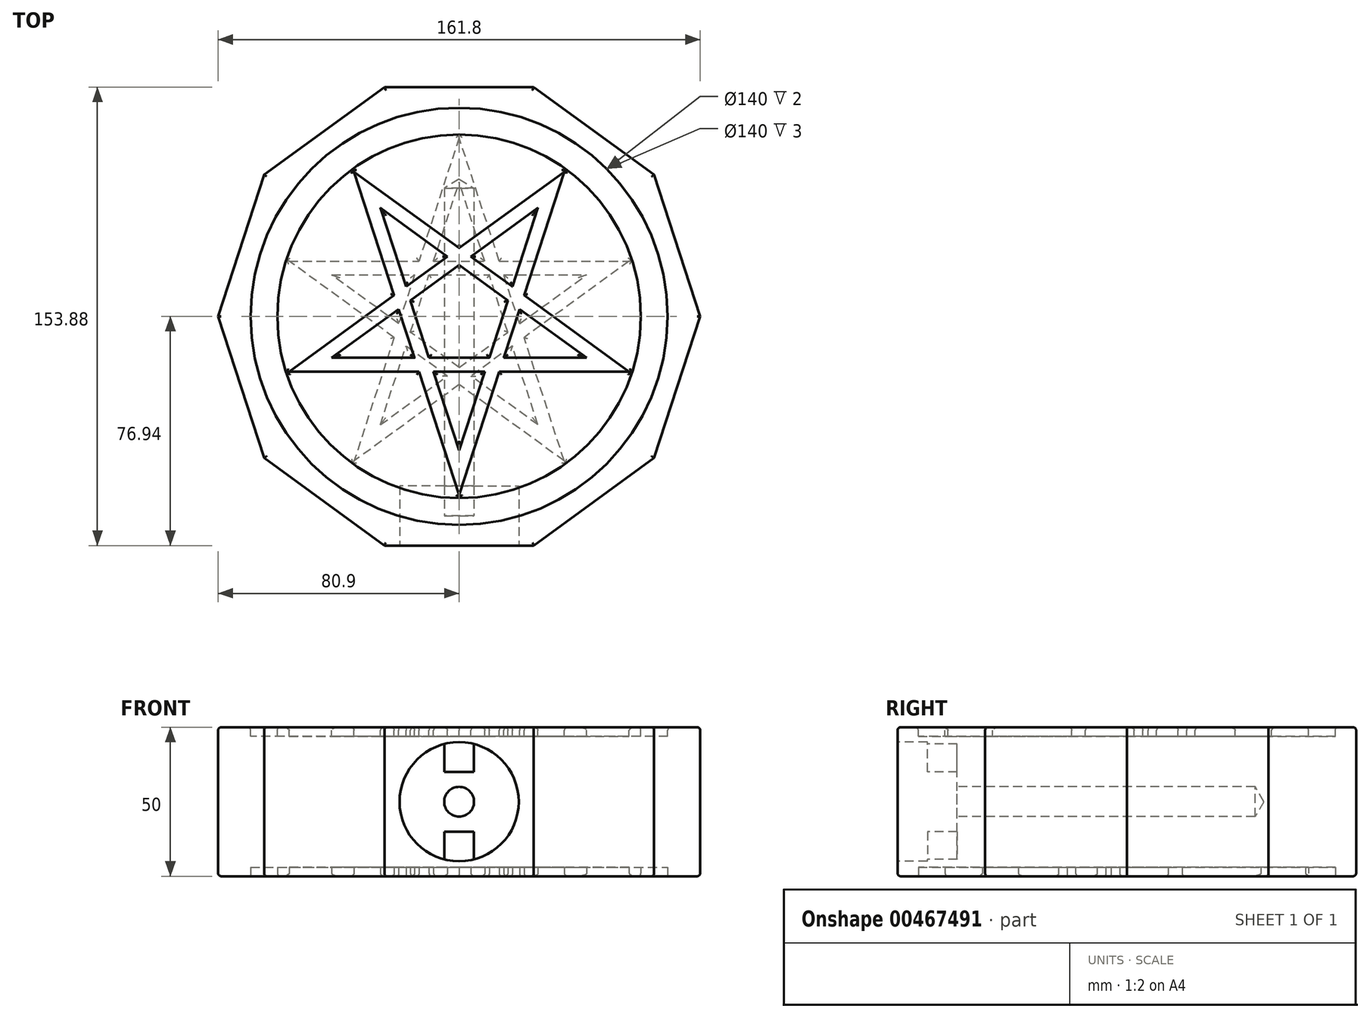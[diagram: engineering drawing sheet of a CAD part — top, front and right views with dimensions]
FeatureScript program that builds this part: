
annotation { "Feature Type Name" : "Feature", "Feature Type Description" : "" }
export const myFeature = defineFeature(function(context is Context, id is Id, definition is map)
    precondition{}
    {
        {
            var Q0;
            Q0=qCreatedBy(makeId("Top.planeOp"),FACE);
            var sketch = newSketch(context, id + "F0", { "sketchPlane" : qUnion([Q0])});
            skCircle(sketch, "E0.cCircle", {"center": v(0, 0) * mm, "radius": 80.9 * mm, "construction": true});
            skLineSegment(sketch, "E0.0", {"start": v(80.9, 0) * mm, "end": v(65.45, -47.55) * mm});
            skLineSegment(sketch, "E0.1", {"start": v(65.45, -47.55) * mm, "end": v(25, -76.94) * mm});
            skLineSegment(sketch, "E0.2", {"start": v(25, -76.94) * mm, "end": v(-25, -76.94) * mm});
            skLineSegment(sketch, "E0.3", {"start": v(-25, -76.94) * mm, "end": v(-65.45, -47.55) * mm});
            skLineSegment(sketch, "E0.4", {"start": v(-65.45, -47.55) * mm, "end": v(-80.9, 0) * mm});
            skLineSegment(sketch, "E0.5", {"start": v(-80.9, 0) * mm, "end": v(-65.45, 47.55) * mm});
            skLineSegment(sketch, "E0.6", {"start": v(-65.45, 47.55) * mm, "end": v(-25, 76.94) * mm});
            skLineSegment(sketch, "E0.7", {"start": v(-25, 76.94) * mm, "end": v(25, 76.94) * mm});
            skLineSegment(sketch, "E0.8", {"start": v(25, 76.94) * mm, "end": v(65.45, 47.55) * mm});
            skLineSegment(sketch, "E0.9", {"start": v(65.45, 47.55) * mm, "end": v(80.9, 0) * mm});
            skSolve(sketch);
        }
        {
            var Q0;
            Q0=makeQuery(id+"F0.imprint","IMPRINT",FACE,{"disambiguationData":[TD([[makeQuery(id+"F0.imprint","IMPRINT",EDGE,{"derivedFrom":sQuery(id+"F0.wireOp",EDGE,"E0.0")}),-1.0]])]});
            extrude(context, id + "F1", {"entities" : qUnion([Q0]), "depth" : 50 * mm});
        }
        {
            var Q0;
            Q0=makeQuery(id+"F1.opExtrude","SWEPT_FACE",FACE,{"disambiguationData":[OSD([sQuery(id+"F0.wireOp",EDGE,"E0.2")])]});
            var sketch = newSketch(context, id + "F2", { "sketchPlane" : qUnion([Q0])});
            skCircle(sketch, "E1", {"center": v(0, 25) * mm, "radius": 20 * mm});
            skLineSegment(sketch, "E2", {"start": v(0, 25) * mm, "end": v(0, 45) * mm, "construction": true});
            skLineSegment(sketch, "E3", {"start": v(0, 25) * mm, "end": v(0, 5) * mm, "construction": true});
            skLineSegment(sketch, "E4", {"start": v(0, 45) * mm, "end": v(0, 35) * mm});
            skLineSegment(sketch, "E5", {"start": v(0, 35) * mm, "end": v(5, 35) * mm});
            skLineSegment(sketch, "E6", {"start": v(5, 35) * mm, "end": v(5, 44.36) * mm});
            skLineSegment(sketch, "E7", {"start": v(0, 35) * mm, "end": v(-5, 35) * mm});
            skLineSegment(sketch, "E8", {"start": v(-5, 35) * mm, "end": v(-5, 44.36) * mm});
            skLineSegment(sketch, "E9", {"start": v(0, 5) * mm, "end": v(0, 15) * mm});
            skLineSegment(sketch, "E10", {"start": v(0, 15) * mm, "end": v(5, 15) * mm});
            skLineSegment(sketch, "E11", {"start": v(5, 15) * mm, "end": v(5, 5.64) * mm});
            skLineSegment(sketch, "E12", {"start": v(0, 15) * mm, "end": v(-5, 15) * mm});
            skLineSegment(sketch, "E13", {"start": v(-5, 15) * mm, "end": v(-5, 5.64) * mm});
            skSolve(sketch);
        }
        {
            var Q0;
            Q0=makeQuery(id+"F2.imprint","IMPRINT",FACE,{"disambiguationData":[TD([[makeQuery(id+"F2.imprint","IMPRINT",EDGE,{"derivedFrom":sQuery(id+"F2.wireOp",EDGE,"E5")}),-1.0]])]});
            extrude(context, id + "F3", {"entities" : qUnion([Q0]), "operationType" : NewBodyOperationType.REMOVE, "oppositeDirection" : true, "depth" : 20 * mm});
        }
        {
            var Q0;
            {var subQ0=sQuery(id+"F2.wireOp",EDGE,"E4");Q0=makeQuery(id+"F2.imprint","IMPRINT",FACE,{"disambiguationData":[TD([[makeQuery(id+"F2.imprint","IMPRINT",EDGE,{"derivedFrom":subQ0}),-1.0]])]});}
            var Q1;
            {var subQ0=sQuery(id+"F2.wireOp",EDGE,"E4");Q1=makeQuery(id+"F2.imprint","IMPRINT",FACE,{"disambiguationData":[TD([[makeQuery(id+"F2.imprint","IMPRINT",EDGE,{"derivedFrom":subQ0}),1.0]])]});}
            var Q2;
            {var subQ0=sQuery(id+"F2.wireOp",EDGE,"E9");Q2=makeQuery(id+"F2.imprint","IMPRINT",FACE,{"disambiguationData":[TD([[makeQuery(id+"F2.imprint","IMPRINT",EDGE,{"derivedFrom":subQ0}),1.0]])]});}
            var Q3;
            {var subQ0=sQuery(id+"F2.wireOp",EDGE,"E9");Q3=makeQuery(id+"F2.imprint","IMPRINT",FACE,{"disambiguationData":[TD([[makeQuery(id+"F2.imprint","IMPRINT",EDGE,{"derivedFrom":subQ0}),-1.0]])]});}
            extrude(context, id + "F4", {"entities" : qUnion([Q0, Q1, Q2, Q3]), "operationType" : NewBodyOperationType.REMOVE, "oppositeDirection" : true, "depth" : 10 * mm});
        }
        {
            var Q0;
            Q0=sQuery(id+"F2.wireOp",VERTEX,"E3.start");
            var Q1;
            Q1=makeQuery(id+"F1.opExtrude","SWEPT_BODY",BODY,{"disambiguationData":[OSD([sQuery(id+"F0.wireOp",EDGE,"E0.0"),sQuery(id+"F0.wireOp",EDGE,"E0.1"),sQuery(id+"F0.wireOp",EDGE,"E0.2"),sQuery(id+"F0.wireOp",EDGE,"E0.3"),sQuery(id+"F0.wireOp",EDGE,"E0.4"),sQuery(id+"F0.wireOp",EDGE,"E0.5"),sQuery(id+"F0.wireOp",EDGE,"E0.6"),sQuery(id+"F0.wireOp",EDGE,"E0.7"),sQuery(id+"F0.wireOp",EDGE,"E0.8"),sQuery(id+"F0.wireOp",EDGE,"E0.9")])]});
            hole(context, id + "F5", {"style" : HoleStyle.SIMPLE, "endStyle" : HoleEndStyle.BLIND, "holeDiameter" : 10 * mm, "holeDepth" : 100 * mm, "isTappedThrough" : true, "tappedDepth" : 12 * mm, "tapClearance" : 3, "locations" : qUnion([Q0]), "scope" : qUnion([Q1])});
        }
        {
            var Q0;
            Q0=makeQuery(id+"F1.opExtrude","CAP_FACE",FACE,{"disambiguationData":[OSD([sQuery(id+"F0.wireOp",EDGE,"E0.0"),sQuery(id+"F0.wireOp",EDGE,"E0.1"),sQuery(id+"F0.wireOp",EDGE,"E0.2"),sQuery(id+"F0.wireOp",EDGE,"E0.3"),sQuery(id+"F0.wireOp",EDGE,"E0.4"),sQuery(id+"F0.wireOp",EDGE,"E0.5"),sQuery(id+"F0.wireOp",EDGE,"E0.6"),sQuery(id+"F0.wireOp",EDGE,"E0.7"),sQuery(id+"F0.wireOp",EDGE,"E0.8"),sQuery(id+"F0.wireOp",EDGE,"E0.9")])],"isStart":false});
            var sketch = newSketch(context, id + "F6", { "sketchPlane" : qUnion([Q0])});
            skCircle(sketch, "E14.cCircle", {"center": v(0, 0) * mm, "radius": 60 * mm});
            skLineSegment(sketch, "E15", {"start": v(-42.8, -13.9) * mm, "end": v(42.8, -13.9) * mm});
            skLineSegment(sketch, "E16", {"start": v(-26.45, 36.4) * mm, "end": v(42.8, -13.9) * mm});
            skLineSegment(sketch, "E17", {"start": v(26.45, 36.4) * mm, "end": v(-42.8, -13.9) * mm});
            skLineSegment(sketch, "E18", {"start": v(-26.45, 36.4) * mm, "end": v(0, -45) * mm});
            skLineSegment(sketch, "E19", {"start": v(26.45, 36.4) * mm, "end": v(0, -45) * mm});
            skLineSegment(sketch, "E20", {"start": v(-57.06, -18.54) * mm, "end": v(57.06, -18.54) * mm});
            skLineSegment(sketch, "E21", {"start": v(57.06, -18.54) * mm, "end": v(-35.27, 48.54) * mm});
            skLineSegment(sketch, "E22", {"start": v(35.27, 48.54) * mm, "end": v(-57.06, -18.54) * mm});
            skLineSegment(sketch, "E23", {"start": v(35.27, 48.54) * mm, "end": v(0, -60) * mm});
            skLineSegment(sketch, "E24", {"start": v(0, -60) * mm, "end": v(-35.27, 48.54) * mm});
            skCircle(sketch, "E25", {"center": v(0, 0) * mm, "radius": 70 * mm});
            skCircle(sketch, "E26", {"center": v(0, 0) * mm, "radius": 61 * mm});
            skSolve(sketch);
        }
        {
            var Q0;
            Q0=makeQuery(id+"F6.imprint","IMPRINT",FACE,{"disambiguationData":[TD([[makeQuery(id+"F6.imprint","IMPRINT",EDGE,{"derivedFrom":sQuery(id+"F6.wireOp",EDGE,"E25")}),1.0]])]});
            var Q1;
            {var subQ5=sQuery(id+"F6.wireOp",EDGE,"E17");var subQ6=sQuery(id+"F6.wireOp",EDGE,"E15");var subQ7=makeQuery(id+"F6.imprint","INTERSECT",VERTEX,{"derivedFrom":[subQ6,subQ5]});Q1=makeQuery(id+"F6.imprint","IMPRINT",FACE,{"disambiguationData":[TD([[makeQuery(id+"F6.imprint","IMPRINT",EDGE,{"disambiguationData":[TD([[subQ7,-1.0]])],"derivedFrom":subQ6}),-1.0]])]});}
            var Q2;
            {var subQ1=sQuery(id+"F6.wireOp",EDGE,"E19");var subQ5=sQuery(id+"F6.wireOp",EDGE,"E18");var subQ9=makeQuery(id+"F6.imprint","INTERSECT",VERTEX,{"derivedFrom":[subQ5,subQ1]});Q2=makeQuery(id+"F6.imprint","IMPRINT",FACE,{"disambiguationData":[TD([[makeQuery(id+"F6.imprint","IMPRINT",EDGE,{"disambiguationData":[TD([[subQ9,1.0]])],"derivedFrom":subQ5}),-1.0]])]});}
            var Q3;
            {var subQ5=sQuery(id+"F6.wireOp",EDGE,"E16");var subQ8=sQuery(id+"F6.wireOp",EDGE,"E15");var subQ9=makeQuery(id+"F6.imprint","INTERSECT",VERTEX,{"derivedFrom":[subQ8,subQ5]});Q3=makeQuery(id+"F6.imprint","IMPRINT",FACE,{"disambiguationData":[TD([[makeQuery(id+"F6.imprint","IMPRINT",EDGE,{"disambiguationData":[TD([[subQ9,1.0]])],"derivedFrom":subQ8}),-1.0]])]});}
            var Q4;
            {var subQ1=sQuery(id+"F6.wireOp",EDGE,"E17");var subQ5=sQuery(id+"F6.wireOp",EDGE,"E19");var subQ9=makeQuery(id+"F6.imprint","INTERSECT",VERTEX,{"derivedFrom":[subQ1,subQ5]});Q4=makeQuery(id+"F6.imprint","IMPRINT",FACE,{"disambiguationData":[TD([[makeQuery(id+"F6.imprint","IMPRINT",EDGE,{"disambiguationData":[TD([[subQ9,-1.0]])],"derivedFrom":subQ1}),-1.0]])]});}
            var Q5;
            {var subQ1=sQuery(id+"F6.wireOp",EDGE,"E16");var subQ7=sQuery(id+"F6.wireOp",EDGE,"E18");var subQ8=makeQuery(id+"F6.imprint","INTERSECT",VERTEX,{"derivedFrom":[subQ1,subQ7]});Q5=makeQuery(id+"F6.imprint","IMPRINT",FACE,{"disambiguationData":[TD([[makeQuery(id+"F6.imprint","IMPRINT",EDGE,{"disambiguationData":[TD([[subQ8,-1.0]])],"derivedFrom":subQ1}),1.0]])]});}
            var Q6;
            {var subQ0=sQuery(id+"F6.wireOp",EDGE,"E18");var subQ1=sQuery(id+"F6.wireOp",EDGE,"E15");var subQ2=makeQuery(id+"F6.imprint","INTERSECT",VERTEX,{"derivedFrom":[subQ1,subQ0]});Q6=makeQuery(id+"F6.imprint","IMPRINT",FACE,{"disambiguationData":[TD([[makeQuery(id+"F6.imprint","IMPRINT",EDGE,{"disambiguationData":[TD([[subQ2,-1.0]])],"derivedFrom":subQ1}),-1.0]])]});}
            var Q7;
            {var subQ0=sQuery(id+"F6.wireOp",EDGE,"E19");var subQ1=sQuery(id+"F6.wireOp",EDGE,"E15");var subQ2=makeQuery(id+"F6.imprint","INTERSECT",VERTEX,{"derivedFrom":[subQ1,subQ0]});Q7=makeQuery(id+"F6.imprint","IMPRINT",FACE,{"disambiguationData":[TD([[makeQuery(id+"F6.imprint","IMPRINT",EDGE,{"disambiguationData":[TD([[subQ2,-1.0]])],"derivedFrom":subQ1}),1.0]])]});}
            var Q8;
            {var subQ0=sQuery(id+"F6.wireOp",EDGE,"E17");var subQ1=sQuery(id+"F6.wireOp",EDGE,"E16");var subQ2=makeQuery(id+"F6.imprint","INTERSECT",VERTEX,{"derivedFrom":[subQ1,subQ0]});Q8=makeQuery(id+"F6.imprint","IMPRINT",FACE,{"disambiguationData":[TD([[makeQuery(id+"F6.imprint","IMPRINT",EDGE,{"disambiguationData":[TD([[subQ2,-1.0]])],"derivedFrom":subQ1}),1.0]])]});}
            var Q9;
            {var subQ0=sQuery(id+"F6.wireOp",EDGE,"E22");var subQ1=sQuery(id+"F6.wireOp",EDGE,"E16");var subQ2=makeQuery(id+"F6.imprint","INTERSECT",VERTEX,{"derivedFrom":[subQ1,subQ0]});Q9=makeQuery(id+"F6.imprint","IMPRINT",FACE,{"disambiguationData":[TD([[makeQuery(id+"F6.imprint","IMPRINT",EDGE,{"disambiguationData":[TD([[subQ2,-1.0]])],"derivedFrom":subQ1}),-1.0]])]});}
            var Q10;
            {var subQ0=sQuery(id+"F6.wireOp",EDGE,"E24");var subQ1=sQuery(id+"F6.wireOp",EDGE,"E15");var subQ2=makeQuery(id+"F6.imprint","INTERSECT",VERTEX,{"derivedFrom":[subQ1,subQ0]});Q10=makeQuery(id+"F6.imprint","IMPRINT",FACE,{"disambiguationData":[TD([[makeQuery(id+"F6.imprint","IMPRINT",EDGE,{"disambiguationData":[TD([[subQ2,-1.0]])],"derivedFrom":subQ1}),1.0]])]});}
            var Q11;
            {var subQ0=sQuery(id+"F6.wireOp",EDGE,"E24");var subQ1=sQuery(id+"F6.wireOp",EDGE,"E15");var subQ2=makeQuery(id+"F6.imprint","INTERSECT",VERTEX,{"derivedFrom":[subQ1,subQ0]});Q11=makeQuery(id+"F6.imprint","IMPRINT",FACE,{"disambiguationData":[TD([[makeQuery(id+"F6.imprint","IMPRINT",EDGE,{"disambiguationData":[TD([[subQ2,-1.0]])],"derivedFrom":subQ1}),-1.0]])]});}
            var Q12;
            {var subQ0=sQuery(id+"F6.wireOp",EDGE,"E18");var subQ1=sQuery(id+"F6.wireOp",EDGE,"E17");var subQ2=makeQuery(id+"F6.imprint","INTERSECT",VERTEX,{"derivedFrom":[subQ1,subQ0]});Q12=makeQuery(id+"F6.imprint","IMPRINT",FACE,{"disambiguationData":[TD([[makeQuery(id+"F6.imprint","IMPRINT",EDGE,{"disambiguationData":[TD([[subQ2,-1.0]])],"derivedFrom":subQ1}),-1.0]])]});}
            var Q13;
            {var subQ0=sQuery(id+"F6.wireOp",EDGE,"E19");var subQ1=sQuery(id+"F6.wireOp",EDGE,"E15");var subQ2=makeQuery(id+"F6.imprint","INTERSECT",VERTEX,{"derivedFrom":[subQ1,subQ0]});Q13=makeQuery(id+"F6.imprint","IMPRINT",FACE,{"disambiguationData":[TD([[makeQuery(id+"F6.imprint","IMPRINT",EDGE,{"disambiguationData":[TD([[subQ2,-1.0]])],"derivedFrom":subQ1}),-1.0]])]});}
            var Q14;
            {var subQ0=sQuery(id+"F6.wireOp",EDGE,"E19");var subQ1=sQuery(id+"F6.wireOp",EDGE,"E16");var subQ2=makeQuery(id+"F6.imprint","INTERSECT",VERTEX,{"derivedFrom":[subQ1,subQ0]});Q14=makeQuery(id+"F6.imprint","IMPRINT",FACE,{"disambiguationData":[TD([[makeQuery(id+"F6.imprint","IMPRINT",EDGE,{"disambiguationData":[TD([[subQ2,-1.0]])],"derivedFrom":subQ1}),1.0]])]});}
            var Q15;
            {var subQ0=sQuery(id+"F6.wireOp",EDGE,"E22");var subQ1=sQuery(id+"F6.wireOp",EDGE,"E16");var subQ2=makeQuery(id+"F6.imprint","INTERSECT",VERTEX,{"derivedFrom":[subQ1,subQ0]});Q15=makeQuery(id+"F6.imprint","IMPRINT",FACE,{"disambiguationData":[TD([[makeQuery(id+"F6.imprint","IMPRINT",EDGE,{"disambiguationData":[TD([[subQ2,-1.0]])],"derivedFrom":subQ1}),1.0]])]});}
            extrude(context, id + "F7", {"entities" : qUnion([Q0, Q1, Q2, Q3, Q4, Q5, Q6, Q7, Q8, Q9, Q10, Q11, Q12, Q13, Q14, Q15]), "operationType" : NewBodyOperationType.REMOVE, "oppositeDirection" : true, "depth" : 3 * mm});
        }
        {
            var Q0;
            Q0=makeQuery(id+"F7.boolean.opBoolean","COPY",EDGE,{"derivedFrom":makeQuery(id+"F7.opExtrude","CAP_EDGE",EDGE,{"disambiguationData":[OSD([sQuery(id+"F6.wireOp",EDGE,"E26")])],"isStart":true})});
            var Q1;
            Q1=makeQuery(id+"F7.boolean.opBoolean","COPY",EDGE,{"derivedFrom":makeQuery(id+"F7.opExtrude","CAP_EDGE",EDGE,{"disambiguationData":[OSD([sQuery(id+"F6.wireOp",EDGE,"E25")])],"isStart":true})});
            var Q2;
            {var subQ0=sQuery(id+"F6.wireOp",EDGE,"E18");var subQ1=sQuery(id+"F6.wireOp",EDGE,"E16");var subQ2=makeQuery(id+"F6.imprint","INTERSECT",VERTEX,{"derivedFrom":[subQ1,subQ0]});Q2=makeQuery(id+"F7.boolean.opBoolean","SPLIT",FACE,{"disambiguationData":[TD([makeQuery(id+"F7.opExtrude","SWEPT_FACE",FACE,{"disambiguationData":[OSD([subQ1]),TDD([makeQuery(id+"F6.imprint","IMPRINT",EDGE,{"disambiguationData":[TD([[subQ2,-1.0]])],"derivedFrom":subQ1})])]})])],"derivedFrom":makeQuery(id+"F1.opExtrude","CAP_FACE",FACE,{"disambiguationData":[OSD([sQuery(id+"F0.wireOp",EDGE,"E0.0"),sQuery(id+"F0.wireOp",EDGE,"E0.1"),sQuery(id+"F0.wireOp",EDGE,"E0.2"),sQuery(id+"F0.wireOp",EDGE,"E0.3"),sQuery(id+"F0.wireOp",EDGE,"E0.4"),sQuery(id+"F0.wireOp",EDGE,"E0.5"),sQuery(id+"F0.wireOp",EDGE,"E0.6"),sQuery(id+"F0.wireOp",EDGE,"E0.7"),sQuery(id+"F0.wireOp",EDGE,"E0.8"),sQuery(id+"F0.wireOp",EDGE,"E0.9")])],"isStart":false})});}
            var Q3;
            {var subQ0=sQuery(id+"F6.wireOp",EDGE,"E18");var subQ1=sQuery(id+"F6.wireOp",EDGE,"E15");var subQ2=makeQuery(id+"F6.imprint","INTERSECT",VERTEX,{"derivedFrom":[subQ1,subQ0]});Q3=makeQuery(id+"F7.boolean.opBoolean","SPLIT",FACE,{"disambiguationData":[TD([makeQuery(id+"F7.opExtrude","SWEPT_FACE",FACE,{"disambiguationData":[OSD([subQ1]),TDD([makeQuery(id+"F6.imprint","IMPRINT",EDGE,{"disambiguationData":[TD([[subQ2,-1.0]])],"derivedFrom":subQ1})])]})])],"derivedFrom":makeQuery(id+"F1.opExtrude","CAP_FACE",FACE,{"disambiguationData":[OSD([sQuery(id+"F0.wireOp",EDGE,"E0.0"),sQuery(id+"F0.wireOp",EDGE,"E0.1"),sQuery(id+"F0.wireOp",EDGE,"E0.2"),sQuery(id+"F0.wireOp",EDGE,"E0.3"),sQuery(id+"F0.wireOp",EDGE,"E0.4"),sQuery(id+"F0.wireOp",EDGE,"E0.5"),sQuery(id+"F0.wireOp",EDGE,"E0.6"),sQuery(id+"F0.wireOp",EDGE,"E0.7"),sQuery(id+"F0.wireOp",EDGE,"E0.8"),sQuery(id+"F0.wireOp",EDGE,"E0.9")])],"isStart":false})});}
            var Q4;
            {var subQ0=sQuery(id+"F6.wireOp",EDGE,"E19");var subQ1=sQuery(id+"F6.wireOp",EDGE,"E17");var subQ2=makeQuery(id+"F6.imprint","INTERSECT",VERTEX,{"derivedFrom":[subQ1,subQ0]});Q4=makeQuery(id+"F7.boolean.opBoolean","SPLIT",FACE,{"disambiguationData":[TD([makeQuery(id+"F7.opExtrude","SWEPT_FACE",FACE,{"disambiguationData":[OSD([subQ1]),TDD([makeQuery(id+"F6.imprint","IMPRINT",EDGE,{"disambiguationData":[TD([[subQ2,-1.0]])],"derivedFrom":subQ1})])]})])],"derivedFrom":makeQuery(id+"F1.opExtrude","CAP_FACE",FACE,{"disambiguationData":[OSD([sQuery(id+"F0.wireOp",EDGE,"E0.0"),sQuery(id+"F0.wireOp",EDGE,"E0.1"),sQuery(id+"F0.wireOp",EDGE,"E0.2"),sQuery(id+"F0.wireOp",EDGE,"E0.3"),sQuery(id+"F0.wireOp",EDGE,"E0.4"),sQuery(id+"F0.wireOp",EDGE,"E0.5"),sQuery(id+"F0.wireOp",EDGE,"E0.6"),sQuery(id+"F0.wireOp",EDGE,"E0.7"),sQuery(id+"F0.wireOp",EDGE,"E0.8"),sQuery(id+"F0.wireOp",EDGE,"E0.9")])],"isStart":false})});}
            var Q5;
            {var subQ0=sQuery(id+"F6.wireOp",EDGE,"E17");var subQ1=sQuery(id+"F6.wireOp",EDGE,"E15");var subQ2=makeQuery(id+"F6.imprint","INTERSECT",VERTEX,{"derivedFrom":[subQ1,subQ0]});Q5=makeQuery(id+"F7.boolean.opBoolean","SPLIT",FACE,{"disambiguationData":[TD([makeQuery(id+"F7.opExtrude","SWEPT_FACE",FACE,{"disambiguationData":[OSD([subQ1]),TDD([makeQuery(id+"F6.imprint","IMPRINT",EDGE,{"disambiguationData":[TD([[subQ2,-1.0]])],"derivedFrom":subQ1})])]})])],"derivedFrom":makeQuery(id+"F1.opExtrude","CAP_FACE",FACE,{"disambiguationData":[OSD([sQuery(id+"F0.wireOp",EDGE,"E0.0"),sQuery(id+"F0.wireOp",EDGE,"E0.1"),sQuery(id+"F0.wireOp",EDGE,"E0.2"),sQuery(id+"F0.wireOp",EDGE,"E0.3"),sQuery(id+"F0.wireOp",EDGE,"E0.4"),sQuery(id+"F0.wireOp",EDGE,"E0.5"),sQuery(id+"F0.wireOp",EDGE,"E0.6"),sQuery(id+"F0.wireOp",EDGE,"E0.7"),sQuery(id+"F0.wireOp",EDGE,"E0.8"),sQuery(id+"F0.wireOp",EDGE,"E0.9")])],"isStart":false})});}
            var Q6;
            {var subQ0=sQuery(id+"F6.wireOp",EDGE,"E16");var subQ1=sQuery(id+"F6.wireOp",EDGE,"E15");var subQ2=makeQuery(id+"F6.imprint","INTERSECT",VERTEX,{"derivedFrom":[subQ1,subQ0]});Q6=makeQuery(id+"F7.boolean.opBoolean","SPLIT",FACE,{"disambiguationData":[TD([makeQuery(id+"F7.opExtrude","SWEPT_FACE",FACE,{"disambiguationData":[OSD([subQ1]),TDD([makeQuery(id+"F6.imprint","IMPRINT",EDGE,{"disambiguationData":[TD([[subQ2,1.0]])],"derivedFrom":subQ1})])]})])],"derivedFrom":makeQuery(id+"F1.opExtrude","CAP_FACE",FACE,{"disambiguationData":[OSD([sQuery(id+"F0.wireOp",EDGE,"E0.0"),sQuery(id+"F0.wireOp",EDGE,"E0.1"),sQuery(id+"F0.wireOp",EDGE,"E0.2"),sQuery(id+"F0.wireOp",EDGE,"E0.3"),sQuery(id+"F0.wireOp",EDGE,"E0.4"),sQuery(id+"F0.wireOp",EDGE,"E0.5"),sQuery(id+"F0.wireOp",EDGE,"E0.6"),sQuery(id+"F0.wireOp",EDGE,"E0.7"),sQuery(id+"F0.wireOp",EDGE,"E0.8"),sQuery(id+"F0.wireOp",EDGE,"E0.9")])],"isStart":false})});}
            var Q7;
            {var subQ0=sQuery(id+"F6.wireOp",EDGE,"E19");var subQ1=sQuery(id+"F6.wireOp",EDGE,"E18");var subQ2=makeQuery(id+"F6.imprint","INTERSECT",VERTEX,{"derivedFrom":[subQ1,subQ0]});Q7=makeQuery(id+"F7.boolean.opBoolean","SPLIT",FACE,{"disambiguationData":[TD([makeQuery(id+"F7.opExtrude","SWEPT_FACE",FACE,{"disambiguationData":[OSD([subQ1]),TDD([makeQuery(id+"F6.imprint","IMPRINT",EDGE,{"disambiguationData":[TD([[subQ2,1.0]])],"derivedFrom":subQ1})])]})])],"derivedFrom":makeQuery(id+"F1.opExtrude","CAP_FACE",FACE,{"disambiguationData":[OSD([sQuery(id+"F0.wireOp",EDGE,"E0.0"),sQuery(id+"F0.wireOp",EDGE,"E0.1"),sQuery(id+"F0.wireOp",EDGE,"E0.2"),sQuery(id+"F0.wireOp",EDGE,"E0.3"),sQuery(id+"F0.wireOp",EDGE,"E0.4"),sQuery(id+"F0.wireOp",EDGE,"E0.5"),sQuery(id+"F0.wireOp",EDGE,"E0.6"),sQuery(id+"F0.wireOp",EDGE,"E0.7"),sQuery(id+"F0.wireOp",EDGE,"E0.8"),sQuery(id+"F0.wireOp",EDGE,"E0.9")])],"isStart":false})});}
            var Q8;
            Q8=makeQuery(id+"F7.boolean.opBoolean","SPLIT",FACE,{"disambiguationData":[TD([makeQuery(id+"F7.opExtrude","SWEPT_FACE",FACE,{"disambiguationData":[OSD([sQuery(id+"F6.wireOp",EDGE,"E26")])]})])],"derivedFrom":makeQuery(id+"F1.opExtrude","CAP_FACE",FACE,{"disambiguationData":[OSD([sQuery(id+"F0.wireOp",EDGE,"E0.0"),sQuery(id+"F0.wireOp",EDGE,"E0.1"),sQuery(id+"F0.wireOp",EDGE,"E0.2"),sQuery(id+"F0.wireOp",EDGE,"E0.3"),sQuery(id+"F0.wireOp",EDGE,"E0.4"),sQuery(id+"F0.wireOp",EDGE,"E0.5"),sQuery(id+"F0.wireOp",EDGE,"E0.6"),sQuery(id+"F0.wireOp",EDGE,"E0.7"),sQuery(id+"F0.wireOp",EDGE,"E0.8"),sQuery(id+"F0.wireOp",EDGE,"E0.9")])],"isStart":false})});
            var Q9;
            {var subQ0=sQuery(id+"F0.wireOp",EDGE,"E0.8");var subQ1=sQuery(id+"F0.wireOp",EDGE,"E0.7");var subQ2=sQuery(id+"F0.wireOp",EDGE,"E0.6");var subQ3=sQuery(id+"F0.wireOp",EDGE,"E0.5");var subQ4=sQuery(id+"F0.wireOp",EDGE,"E0.4");var subQ5=sQuery(id+"F0.wireOp",EDGE,"E0.9");var subQ6=sQuery(id+"F0.wireOp",EDGE,"E0.0");var subQ7=sQuery(id+"F0.wireOp",EDGE,"E0.3");var subQ8=sQuery(id+"F0.wireOp",EDGE,"E0.1");var subQ9=sQuery(id+"F0.wireOp",EDGE,"E0.2");Q9=makeQuery(id+"F7.boolean.opBoolean","SPLIT",FACE,{"disambiguationData":[TD([makeQuery(id+"F1.opExtrude","SWEPT_FACE",FACE,{"disambiguationData":[OSD([subQ6])]})])],"derivedFrom":makeQuery(id+"F1.opExtrude","CAP_FACE",FACE,{"disambiguationData":[OSD([subQ6,subQ8,subQ9,subQ7,subQ4,subQ3,subQ2,subQ1,subQ0,subQ5])],"isStart":false})});}
            var Q10;
            Q10=makeQuery(id+"F1.opExtrude","CAP_FACE",FACE,{"disambiguationData":[OSD([sQuery(id+"F0.wireOp",EDGE,"E0.0"),sQuery(id+"F0.wireOp",EDGE,"E0.1"),sQuery(id+"F0.wireOp",EDGE,"E0.2"),sQuery(id+"F0.wireOp",EDGE,"E0.3"),sQuery(id+"F0.wireOp",EDGE,"E0.4"),sQuery(id+"F0.wireOp",EDGE,"E0.5"),sQuery(id+"F0.wireOp",EDGE,"E0.6"),sQuery(id+"F0.wireOp",EDGE,"E0.7"),sQuery(id+"F0.wireOp",EDGE,"E0.8"),sQuery(id+"F0.wireOp",EDGE,"E0.9")])],"isStart":true});
            fillet(context, id + "F8", {"entities" : qUnion([Q0, Q1, Q2, Q3, Q4, Q5, Q6, Q7, Q8, Q9, Q10]), "radius" : 1 * mm, "tangentPropagation" : true, "allowEdgeOverflow" : false});
        }
        {
            var Q0;
            Q0=makeQuery(id+"F1.opExtrude","CAP_FACE",FACE,{"disambiguationData":[OSD([sQuery(id+"F0.wireOp",EDGE,"E0.0"),sQuery(id+"F0.wireOp",EDGE,"E0.1"),sQuery(id+"F0.wireOp",EDGE,"E0.2"),sQuery(id+"F0.wireOp",EDGE,"E0.3"),sQuery(id+"F0.wireOp",EDGE,"E0.4"),sQuery(id+"F0.wireOp",EDGE,"E0.5"),sQuery(id+"F0.wireOp",EDGE,"E0.6"),sQuery(id+"F0.wireOp",EDGE,"E0.7"),sQuery(id+"F0.wireOp",EDGE,"E0.8"),sQuery(id+"F0.wireOp",EDGE,"E0.9")])],"isStart":true});
            var sketch = newSketch(context, id + "F9", { "sketchPlane" : qUnion([Q0])});
            skCircle(sketch, "E27.cCircle", {"center": v(0, 0) * mm, "radius": 60 * mm});
            skLineSegment(sketch, "E28", {"start": v(-42.8, -13.9) * mm, "end": v(42.8, -13.9) * mm});
            skLineSegment(sketch, "E29", {"start": v(-26.45, 36.4) * mm, "end": v(42.8, -13.9) * mm});
            skLineSegment(sketch, "E30", {"start": v(26.45, 36.4) * mm, "end": v(-42.8, -13.9) * mm});
            skLineSegment(sketch, "E31", {"start": v(-26.45, 36.4) * mm, "end": v(0, -45) * mm});
            skLineSegment(sketch, "E32", {"start": v(26.45, 36.4) * mm, "end": v(0, -45) * mm});
            skLineSegment(sketch, "E33", {"start": v(-57.06, -18.54) * mm, "end": v(57.06, -18.54) * mm});
            skLineSegment(sketch, "E34", {"start": v(57.06, -18.54) * mm, "end": v(-35.27, 48.54) * mm});
            skLineSegment(sketch, "E35", {"start": v(35.27, 48.54) * mm, "end": v(-57.06, -18.54) * mm});
            skLineSegment(sketch, "E36", {"start": v(35.27, 48.54) * mm, "end": v(0, -60) * mm});
            skLineSegment(sketch, "E37", {"start": v(0, -60) * mm, "end": v(-35.27, 48.54) * mm});
            skCircle(sketch, "E38", {"center": v(0, 0) * mm, "radius": 70 * mm});
            skCircle(sketch, "E39", {"center": v(0, 0) * mm, "radius": 61 * mm});
            skSolve(sketch);
        }
        {
            var Q0;
            Q0=makeQuery(id+"F9.imprint","IMPRINT",FACE,{"disambiguationData":[TD([[makeQuery(id+"F9.imprint","IMPRINT",EDGE,{"derivedFrom":sQuery(id+"F9.wireOp",EDGE,"E38")}),1.0]])]});
            var Q1;
            {var subQ5=sQuery(id+"F9.wireOp",EDGE,"E29");var subQ8=sQuery(id+"F9.wireOp",EDGE,"E28");var subQ9=makeQuery(id+"F9.imprint","INTERSECT",VERTEX,{"derivedFrom":[subQ8,subQ5]});Q1=makeQuery(id+"F9.imprint","IMPRINT",FACE,{"disambiguationData":[TD([[makeQuery(id+"F9.imprint","IMPRINT",EDGE,{"disambiguationData":[TD([[subQ9,1.0]])],"derivedFrom":subQ8}),-1.0]])]});}
            var Q2;
            {var subQ1=sQuery(id+"F9.wireOp",EDGE,"E32");var subQ5=sQuery(id+"F9.wireOp",EDGE,"E31");var subQ9=makeQuery(id+"F9.imprint","INTERSECT",VERTEX,{"derivedFrom":[subQ5,subQ1]});Q2=makeQuery(id+"F9.imprint","IMPRINT",FACE,{"disambiguationData":[TD([[makeQuery(id+"F9.imprint","IMPRINT",EDGE,{"disambiguationData":[TD([[subQ9,1.0]])],"derivedFrom":subQ5}),-1.0]])]});}
            var Q3;
            {var subQ1=sQuery(id+"F9.wireOp",EDGE,"E30");var subQ5=sQuery(id+"F9.wireOp",EDGE,"E32");var subQ9=makeQuery(id+"F9.imprint","INTERSECT",VERTEX,{"derivedFrom":[subQ1,subQ5]});Q3=makeQuery(id+"F9.imprint","IMPRINT",FACE,{"disambiguationData":[TD([[makeQuery(id+"F9.imprint","IMPRINT",EDGE,{"disambiguationData":[TD([[subQ9,-1.0]])],"derivedFrom":subQ1}),-1.0]])]});}
            var Q4;
            {var subQ1=sQuery(id+"F9.wireOp",EDGE,"E29");var subQ7=sQuery(id+"F9.wireOp",EDGE,"E31");var subQ8=makeQuery(id+"F9.imprint","INTERSECT",VERTEX,{"derivedFrom":[subQ1,subQ7]});Q4=makeQuery(id+"F9.imprint","IMPRINT",FACE,{"disambiguationData":[TD([[makeQuery(id+"F9.imprint","IMPRINT",EDGE,{"disambiguationData":[TD([[subQ8,-1.0]])],"derivedFrom":subQ1}),1.0]])]});}
            var Q5;
            {var subQ5=sQuery(id+"F9.wireOp",EDGE,"E30");var subQ6=sQuery(id+"F9.wireOp",EDGE,"E28");var subQ7=makeQuery(id+"F9.imprint","INTERSECT",VERTEX,{"derivedFrom":[subQ6,subQ5]});Q5=makeQuery(id+"F9.imprint","IMPRINT",FACE,{"disambiguationData":[TD([[makeQuery(id+"F9.imprint","IMPRINT",EDGE,{"disambiguationData":[TD([[subQ7,-1.0]])],"derivedFrom":subQ6}),-1.0]])]});}
            var Q6;
            {var subQ0=sQuery(id+"F9.wireOp",EDGE,"E37");var subQ1=sQuery(id+"F9.wireOp",EDGE,"E28");var subQ2=makeQuery(id+"F9.imprint","INTERSECT",VERTEX,{"derivedFrom":[subQ1,subQ0]});Q6=makeQuery(id+"F9.imprint","IMPRINT",FACE,{"disambiguationData":[TD([[makeQuery(id+"F9.imprint","IMPRINT",EDGE,{"disambiguationData":[TD([[subQ2,-1.0]])],"derivedFrom":subQ1}),1.0]])]});}
            var Q7;
            {var subQ0=sQuery(id+"F9.wireOp",EDGE,"E32");var subQ1=sQuery(id+"F9.wireOp",EDGE,"E28");var subQ2=makeQuery(id+"F9.imprint","INTERSECT",VERTEX,{"derivedFrom":[subQ1,subQ0]});Q7=makeQuery(id+"F9.imprint","IMPRINT",FACE,{"disambiguationData":[TD([[makeQuery(id+"F9.imprint","IMPRINT",EDGE,{"disambiguationData":[TD([[subQ2,-1.0]])],"derivedFrom":subQ1}),1.0]])]});}
            var Q8;
            {var subQ0=sQuery(id+"F9.wireOp",EDGE,"E31");var subQ1=sQuery(id+"F9.wireOp",EDGE,"E28");var subQ2=makeQuery(id+"F9.imprint","INTERSECT",VERTEX,{"derivedFrom":[subQ1,subQ0]});Q8=makeQuery(id+"F9.imprint","IMPRINT",FACE,{"disambiguationData":[TD([[makeQuery(id+"F9.imprint","IMPRINT",EDGE,{"disambiguationData":[TD([[subQ2,-1.0]])],"derivedFrom":subQ1}),-1.0]])]});}
            var Q9;
            {var subQ0=sQuery(id+"F9.wireOp",EDGE,"E30");var subQ1=sQuery(id+"F9.wireOp",EDGE,"E29");var subQ2=makeQuery(id+"F9.imprint","INTERSECT",VERTEX,{"derivedFrom":[subQ1,subQ0]});Q9=makeQuery(id+"F9.imprint","IMPRINT",FACE,{"disambiguationData":[TD([[makeQuery(id+"F9.imprint","IMPRINT",EDGE,{"disambiguationData":[TD([[subQ2,-1.0]])],"derivedFrom":subQ1}),1.0]])]});}
            var Q10;
            {var subQ0=sQuery(id+"F9.wireOp",EDGE,"E35");var subQ1=sQuery(id+"F9.wireOp",EDGE,"E29");var subQ2=makeQuery(id+"F9.imprint","INTERSECT",VERTEX,{"derivedFrom":[subQ1,subQ0]});Q10=makeQuery(id+"F9.imprint","IMPRINT",FACE,{"disambiguationData":[TD([[makeQuery(id+"F9.imprint","IMPRINT",EDGE,{"disambiguationData":[TD([[subQ2,-1.0]])],"derivedFrom":subQ1}),-1.0]])]});}
            var Q11;
            {var subQ0=sQuery(id+"F9.wireOp",EDGE,"E32");var subQ1=sQuery(id+"F9.wireOp",EDGE,"E29");var subQ2=makeQuery(id+"F9.imprint","INTERSECT",VERTEX,{"derivedFrom":[subQ1,subQ0]});Q11=makeQuery(id+"F9.imprint","IMPRINT",FACE,{"disambiguationData":[TD([[makeQuery(id+"F9.imprint","IMPRINT",EDGE,{"disambiguationData":[TD([[subQ2,-1.0]])],"derivedFrom":subQ1}),1.0]])]});}
            var Q12;
            {var subQ0=sQuery(id+"F9.wireOp",EDGE,"E32");var subQ1=sQuery(id+"F9.wireOp",EDGE,"E28");var subQ2=makeQuery(id+"F9.imprint","INTERSECT",VERTEX,{"derivedFrom":[subQ1,subQ0]});Q12=makeQuery(id+"F9.imprint","IMPRINT",FACE,{"disambiguationData":[TD([[makeQuery(id+"F9.imprint","IMPRINT",EDGE,{"disambiguationData":[TD([[subQ2,-1.0]])],"derivedFrom":subQ1}),-1.0]])]});}
            var Q13;
            {var subQ0=sQuery(id+"F9.wireOp",EDGE,"E37");var subQ1=sQuery(id+"F9.wireOp",EDGE,"E28");var subQ2=makeQuery(id+"F9.imprint","INTERSECT",VERTEX,{"derivedFrom":[subQ1,subQ0]});Q13=makeQuery(id+"F9.imprint","IMPRINT",FACE,{"disambiguationData":[TD([[makeQuery(id+"F9.imprint","IMPRINT",EDGE,{"disambiguationData":[TD([[subQ2,-1.0]])],"derivedFrom":subQ1}),-1.0]])]});}
            var Q14;
            {var subQ0=sQuery(id+"F9.wireOp",EDGE,"E31");var subQ1=sQuery(id+"F9.wireOp",EDGE,"E30");var subQ2=makeQuery(id+"F9.imprint","INTERSECT",VERTEX,{"derivedFrom":[subQ1,subQ0]});Q14=makeQuery(id+"F9.imprint","IMPRINT",FACE,{"disambiguationData":[TD([[makeQuery(id+"F9.imprint","IMPRINT",EDGE,{"disambiguationData":[TD([[subQ2,-1.0]])],"derivedFrom":subQ1}),-1.0]])]});}
            var Q15;
            {var subQ0=sQuery(id+"F9.wireOp",EDGE,"E35");var subQ1=sQuery(id+"F9.wireOp",EDGE,"E29");var subQ2=makeQuery(id+"F9.imprint","INTERSECT",VERTEX,{"derivedFrom":[subQ1,subQ0]});Q15=makeQuery(id+"F9.imprint","IMPRINT",FACE,{"disambiguationData":[TD([[makeQuery(id+"F9.imprint","IMPRINT",EDGE,{"disambiguationData":[TD([[subQ2,-1.0]])],"derivedFrom":subQ1}),1.0]])]});}
            extrude(context, id + "F10", {"entities" : qUnion([Q0, Q1, Q2, Q3, Q4, Q5, Q6, Q7, Q8, Q9, Q10, Q11, Q12, Q13, Q14, Q15]), "operationType" : NewBodyOperationType.REMOVE, "oppositeDirection" : true, "depth" : 3 * mm});
        }
        {
            var Q0;
            {var subQ0=sQuery(id+"F9.wireOp",EDGE,"E33");Q0=makeQuery(id+"F10.boolean.opBoolean","COPY",EDGE,{"derivedFrom":makeQuery(id+"F10.opExtrude","CAP_EDGE",EDGE,{"disambiguationData":[OSD([subQ0]),TDD([makeQuery(id+"F9.imprint","IMPRINT",EDGE,{"disambiguationData":[TD([[makeQuery(id+"F9.imprint","INTERSECT",VERTEX,{"derivedFrom":[subQ0,sQuery(id+"F9.wireOp",EDGE,"E36")]}),-1.0]])],"derivedFrom":subQ0})])],"isStart":true})});}
            var Q1;
            {var subQ0=sQuery(id+"F9.wireOp",EDGE,"E36");Q1=makeQuery(id+"F10.boolean.opBoolean","COPY",EDGE,{"derivedFrom":makeQuery(id+"F10.opExtrude","CAP_EDGE",EDGE,{"disambiguationData":[OSD([subQ0]),TDD([makeQuery(id+"F9.imprint","IMPRINT",EDGE,{"disambiguationData":[TD([[makeQuery(id+"F9.imprint","INTERSECT",VERTEX,{"derivedFrom":[sQuery(id+"F9.wireOp",EDGE,"E33"),subQ0]}),-1.0]])],"derivedFrom":subQ0})])],"isStart":true})});}
            var Q2;
            {var subQ0=sQuery(id+"F9.wireOp",EDGE,"E37");Q2=makeQuery(id+"F10.boolean.opBoolean","COPY",EDGE,{"derivedFrom":makeQuery(id+"F10.opExtrude","CAP_EDGE",EDGE,{"disambiguationData":[OSD([subQ0]),TDD([makeQuery(id+"F9.imprint","IMPRINT",EDGE,{"disambiguationData":[TD([[makeQuery(id+"F9.imprint","INTERSECT",VERTEX,{"derivedFrom":[sQuery(id+"F9.wireOp",EDGE,"E33"),subQ0]}),1.0]])],"derivedFrom":subQ0})])],"isStart":true})});}
            var Q3;
            {var subQ0=sQuery(id+"F9.wireOp",EDGE,"E32");var subQ1=sQuery(id+"F9.wireOp",EDGE,"E31");var subQ2=makeQuery(id+"F9.imprint","INTERSECT",VERTEX,{"derivedFrom":[subQ1,subQ0]});Q3=makeQuery(id+"F10.boolean.opBoolean","SPLIT",FACE,{"disambiguationData":[TD([makeQuery(id+"F10.opExtrude","SWEPT_FACE",FACE,{"disambiguationData":[OSD([subQ1]),TDD([makeQuery(id+"F9.imprint","IMPRINT",EDGE,{"disambiguationData":[TD([[subQ2,1.0]])],"derivedFrom":subQ1})])]})])],"derivedFrom":makeQuery(id+"F1.opExtrude","CAP_FACE",FACE,{"disambiguationData":[OSD([sQuery(id+"F0.wireOp",EDGE,"E0.0"),sQuery(id+"F0.wireOp",EDGE,"E0.1"),sQuery(id+"F0.wireOp",EDGE,"E0.2"),sQuery(id+"F0.wireOp",EDGE,"E0.3"),sQuery(id+"F0.wireOp",EDGE,"E0.4"),sQuery(id+"F0.wireOp",EDGE,"E0.5"),sQuery(id+"F0.wireOp",EDGE,"E0.6"),sQuery(id+"F0.wireOp",EDGE,"E0.7"),sQuery(id+"F0.wireOp",EDGE,"E0.8"),sQuery(id+"F0.wireOp",EDGE,"E0.9")])],"isStart":true})});}
            var Q4;
            Q4=makeQuery(id+"F10.boolean.opBoolean","SPLIT",FACE,{"disambiguationData":[TD([makeQuery(id+"F10.opExtrude","SWEPT_FACE",FACE,{"disambiguationData":[OSD([sQuery(id+"F9.wireOp",EDGE,"E39")])]})])],"derivedFrom":makeQuery(id+"F1.opExtrude","CAP_FACE",FACE,{"disambiguationData":[OSD([sQuery(id+"F0.wireOp",EDGE,"E0.0"),sQuery(id+"F0.wireOp",EDGE,"E0.1"),sQuery(id+"F0.wireOp",EDGE,"E0.2"),sQuery(id+"F0.wireOp",EDGE,"E0.3"),sQuery(id+"F0.wireOp",EDGE,"E0.4"),sQuery(id+"F0.wireOp",EDGE,"E0.5"),sQuery(id+"F0.wireOp",EDGE,"E0.6"),sQuery(id+"F0.wireOp",EDGE,"E0.7"),sQuery(id+"F0.wireOp",EDGE,"E0.8"),sQuery(id+"F0.wireOp",EDGE,"E0.9")])],"isStart":true})});
            var Q5;
            {var subQ0=sQuery(id+"F9.wireOp",EDGE,"E30");var subQ1=sQuery(id+"F9.wireOp",EDGE,"E28");var subQ2=makeQuery(id+"F9.imprint","INTERSECT",VERTEX,{"derivedFrom":[subQ1,subQ0]});Q5=makeQuery(id+"F10.boolean.opBoolean","SPLIT",FACE,{"disambiguationData":[TD([makeQuery(id+"F10.opExtrude","SWEPT_FACE",FACE,{"disambiguationData":[OSD([subQ1]),TDD([makeQuery(id+"F9.imprint","IMPRINT",EDGE,{"disambiguationData":[TD([[subQ2,-1.0]])],"derivedFrom":subQ1})])]})])],"derivedFrom":makeQuery(id+"F1.opExtrude","CAP_FACE",FACE,{"disambiguationData":[OSD([sQuery(id+"F0.wireOp",EDGE,"E0.0"),sQuery(id+"F0.wireOp",EDGE,"E0.1"),sQuery(id+"F0.wireOp",EDGE,"E0.2"),sQuery(id+"F0.wireOp",EDGE,"E0.3"),sQuery(id+"F0.wireOp",EDGE,"E0.4"),sQuery(id+"F0.wireOp",EDGE,"E0.5"),sQuery(id+"F0.wireOp",EDGE,"E0.6"),sQuery(id+"F0.wireOp",EDGE,"E0.7"),sQuery(id+"F0.wireOp",EDGE,"E0.8"),sQuery(id+"F0.wireOp",EDGE,"E0.9")])],"isStart":true})});}
            var Q6;
            {var subQ0=sQuery(id+"F9.wireOp",EDGE,"E31");var subQ1=sQuery(id+"F9.wireOp",EDGE,"E28");var subQ2=makeQuery(id+"F9.imprint","INTERSECT",VERTEX,{"derivedFrom":[subQ1,subQ0]});Q6=makeQuery(id+"F10.boolean.opBoolean","SPLIT",FACE,{"disambiguationData":[TD([makeQuery(id+"F10.opExtrude","SWEPT_FACE",FACE,{"disambiguationData":[OSD([subQ1]),TDD([makeQuery(id+"F9.imprint","IMPRINT",EDGE,{"disambiguationData":[TD([[subQ2,-1.0]])],"derivedFrom":subQ1})])]})])],"derivedFrom":makeQuery(id+"F1.opExtrude","CAP_FACE",FACE,{"disambiguationData":[OSD([sQuery(id+"F0.wireOp",EDGE,"E0.0"),sQuery(id+"F0.wireOp",EDGE,"E0.1"),sQuery(id+"F0.wireOp",EDGE,"E0.2"),sQuery(id+"F0.wireOp",EDGE,"E0.3"),sQuery(id+"F0.wireOp",EDGE,"E0.4"),sQuery(id+"F0.wireOp",EDGE,"E0.5"),sQuery(id+"F0.wireOp",EDGE,"E0.6"),sQuery(id+"F0.wireOp",EDGE,"E0.7"),sQuery(id+"F0.wireOp",EDGE,"E0.8"),sQuery(id+"F0.wireOp",EDGE,"E0.9")])],"isStart":true})});}
            var Q7;
            {var subQ0=sQuery(id+"F9.wireOp",EDGE,"E29");var subQ1=sQuery(id+"F9.wireOp",EDGE,"E28");var subQ2=makeQuery(id+"F9.imprint","INTERSECT",VERTEX,{"derivedFrom":[subQ1,subQ0]});Q7=makeQuery(id+"F10.boolean.opBoolean","SPLIT",FACE,{"disambiguationData":[TD([makeQuery(id+"F10.opExtrude","SWEPT_FACE",FACE,{"disambiguationData":[OSD([subQ1]),TDD([makeQuery(id+"F9.imprint","IMPRINT",EDGE,{"disambiguationData":[TD([[subQ2,1.0]])],"derivedFrom":subQ1})])]})])],"derivedFrom":makeQuery(id+"F1.opExtrude","CAP_FACE",FACE,{"disambiguationData":[OSD([sQuery(id+"F0.wireOp",EDGE,"E0.0"),sQuery(id+"F0.wireOp",EDGE,"E0.1"),sQuery(id+"F0.wireOp",EDGE,"E0.2"),sQuery(id+"F0.wireOp",EDGE,"E0.3"),sQuery(id+"F0.wireOp",EDGE,"E0.4"),sQuery(id+"F0.wireOp",EDGE,"E0.5"),sQuery(id+"F0.wireOp",EDGE,"E0.6"),sQuery(id+"F0.wireOp",EDGE,"E0.7"),sQuery(id+"F0.wireOp",EDGE,"E0.8"),sQuery(id+"F0.wireOp",EDGE,"E0.9")])],"isStart":true})});}
            var Q8;
            {var subQ0=sQuery(id+"F9.wireOp",EDGE,"E32");var subQ1=sQuery(id+"F9.wireOp",EDGE,"E30");var subQ2=makeQuery(id+"F9.imprint","INTERSECT",VERTEX,{"derivedFrom":[subQ1,subQ0]});Q8=makeQuery(id+"F10.boolean.opBoolean","SPLIT",FACE,{"disambiguationData":[TD([makeQuery(id+"F10.opExtrude","SWEPT_FACE",FACE,{"disambiguationData":[OSD([subQ1]),TDD([makeQuery(id+"F9.imprint","IMPRINT",EDGE,{"disambiguationData":[TD([[subQ2,-1.0]])],"derivedFrom":subQ1})])]})])],"derivedFrom":makeQuery(id+"F1.opExtrude","CAP_FACE",FACE,{"disambiguationData":[OSD([sQuery(id+"F0.wireOp",EDGE,"E0.0"),sQuery(id+"F0.wireOp",EDGE,"E0.1"),sQuery(id+"F0.wireOp",EDGE,"E0.2"),sQuery(id+"F0.wireOp",EDGE,"E0.3"),sQuery(id+"F0.wireOp",EDGE,"E0.4"),sQuery(id+"F0.wireOp",EDGE,"E0.5"),sQuery(id+"F0.wireOp",EDGE,"E0.6"),sQuery(id+"F0.wireOp",EDGE,"E0.7"),sQuery(id+"F0.wireOp",EDGE,"E0.8"),sQuery(id+"F0.wireOp",EDGE,"E0.9")])],"isStart":true})});}
            var Q9;
            {var subQ0=sQuery(id+"F9.wireOp",EDGE,"E31");var subQ1=sQuery(id+"F9.wireOp",EDGE,"E29");var subQ2=makeQuery(id+"F9.imprint","INTERSECT",VERTEX,{"derivedFrom":[subQ1,subQ0]});Q9=makeQuery(id+"F10.boolean.opBoolean","SPLIT",FACE,{"disambiguationData":[TD([makeQuery(id+"F10.opExtrude","SWEPT_FACE",FACE,{"disambiguationData":[OSD([subQ1]),TDD([makeQuery(id+"F9.imprint","IMPRINT",EDGE,{"disambiguationData":[TD([[subQ2,-1.0]])],"derivedFrom":subQ1})])]})])],"derivedFrom":makeQuery(id+"F1.opExtrude","CAP_FACE",FACE,{"disambiguationData":[OSD([sQuery(id+"F0.wireOp",EDGE,"E0.0"),sQuery(id+"F0.wireOp",EDGE,"E0.1"),sQuery(id+"F0.wireOp",EDGE,"E0.2"),sQuery(id+"F0.wireOp",EDGE,"E0.3"),sQuery(id+"F0.wireOp",EDGE,"E0.4"),sQuery(id+"F0.wireOp",EDGE,"E0.5"),sQuery(id+"F0.wireOp",EDGE,"E0.6"),sQuery(id+"F0.wireOp",EDGE,"E0.7"),sQuery(id+"F0.wireOp",EDGE,"E0.8"),sQuery(id+"F0.wireOp",EDGE,"E0.9")])],"isStart":true})});}
            var Q10;
            Q10=makeQuery(id+"F10.boolean.opBoolean","COPY",EDGE,{"derivedFrom":makeQuery(id+"F10.opExtrude","CAP_EDGE",EDGE,{"disambiguationData":[OSD([sQuery(id+"F9.wireOp",EDGE,"E38")])],"isStart":true})});
            fillet(context, id + "F11", {"entities" : qUnion([Q0, Q1, Q2, Q3, Q4, Q5, Q6, Q7, Q8, Q9, Q10]), "radius" : 1 * mm, "tangentPropagation" : true, "allowEdgeOverflow" : false});
        }
    });
